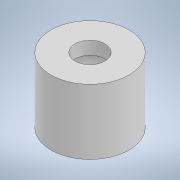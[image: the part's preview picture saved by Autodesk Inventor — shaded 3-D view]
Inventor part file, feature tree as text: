
AUTODESK INVENTOR PART (.ipt)
format: ipt  version: 2022 (Build 260153000, 153)  size: 109,568 bytes
history: native  units: mm
features: extrude x3, sketch x3
ambient origin geometry x8: Origin, YZ Plane, XZ Plane, XY Plane, X Axis, Y Axis, Z Axis, Center Point
bodies: Solid1 (feature_tree)
feature tree (6):
  extrude  "Extrusion1"  Depth=5.0mm TaperAngle=0.0deg
  extrude  "Extrusion3"  Depth=4.0mm TaperAngle=0.0deg
  extrude  "Extrusion4"  TaperAngle=0.0deg  [1 undecoded]
  sketch  "Sketch1"  dims[d0=6.0mm d1=5.0mm d2=0.0mm]
  sketch  "Sketch3"  dims[d6=0.8mm d7=4.0mm d8=0.0mm]
  sketch  "Sketch4"  dims[d9=2.3mm d10=0.0mm d11=0.0mm]
note: 1 required parameter value undecoded (feature->parameter linkage not recoverable at this tier; creation-order binding heuristic only, values carry confidence <= 0.55)
